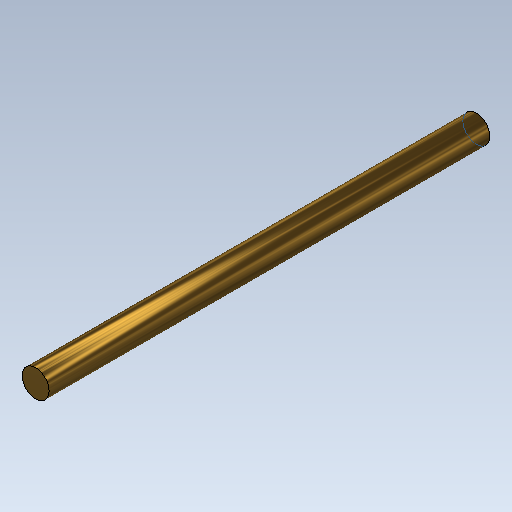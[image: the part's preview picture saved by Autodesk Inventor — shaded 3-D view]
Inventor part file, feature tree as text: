
AUTODESK INVENTOR PART (.ipt)
format: ipt  version: 2020 (Build 240168000, 168)  size: 103,936 bytes
history: native  units: mm
features: other x1, extrude x1, sketch x1
ambient origin geometry x8: Origin, YZ Plane, XZ Plane, XY Plane, X Axis, Y Axis, Z Axis, Center Point
bodies: Body1 (feature_tree)
feature tree (3):
  other  "ソリッド1"
  extrude  "押し出し1"  Depth=3.0mm
  sketch  "スケッチ1"
